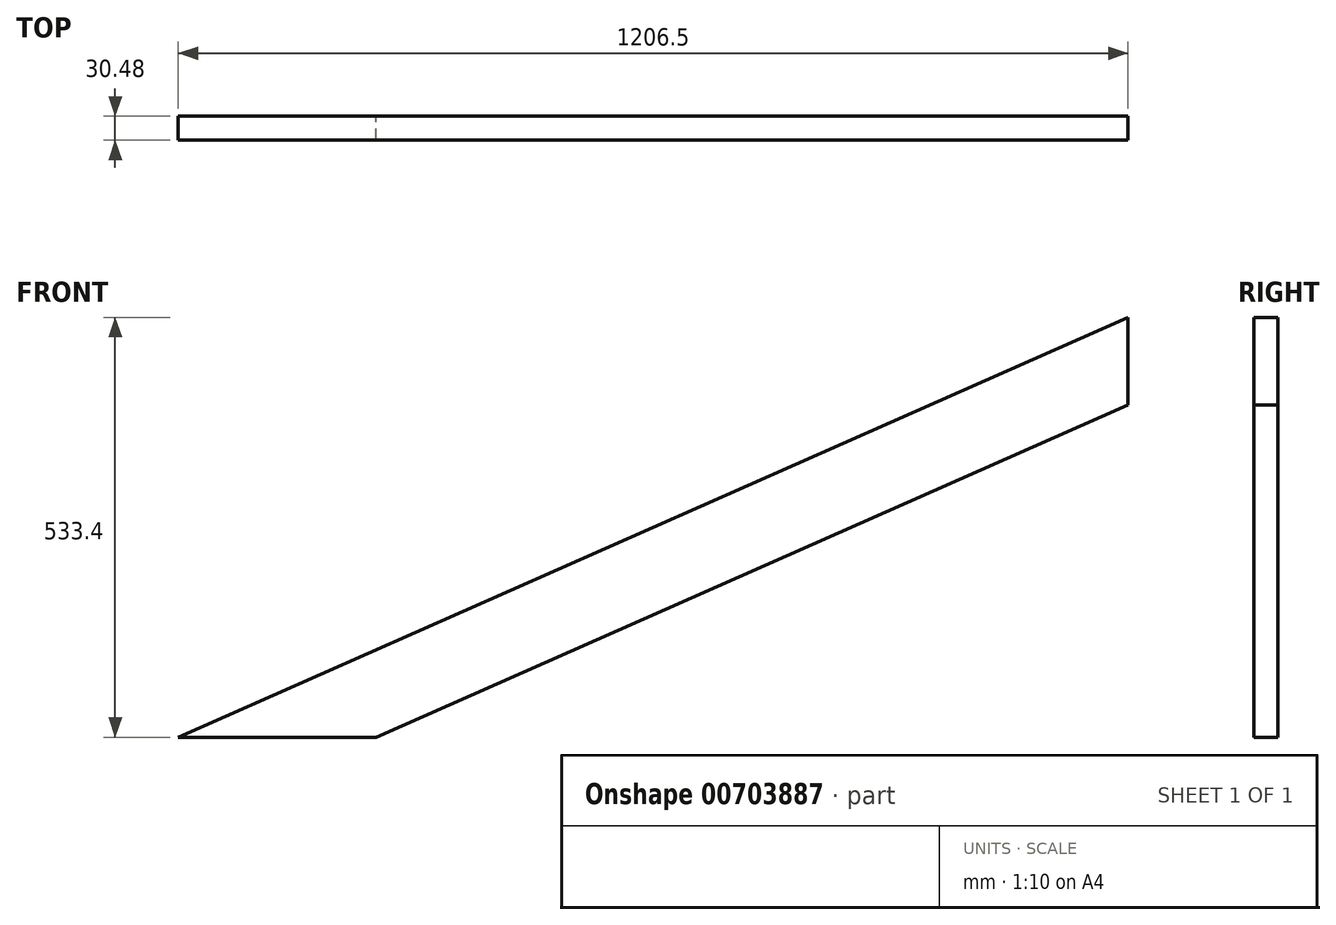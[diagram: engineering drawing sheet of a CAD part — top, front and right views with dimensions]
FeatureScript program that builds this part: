
annotation { "Feature Type Name" : "Feature", "Feature Type Description" : "" }
export const myFeature = defineFeature(function(context is Context, id is Id, definition is map)
    precondition{}
    {
        {
            var Q0;
            Q0=qCreatedBy(makeId("Front.planeOp"),FACE);
            var sketch = newSketch(context, id + "F0", { "sketchPlane" : qUnion([Q0])});
            skLineSegment(sketch, "E0", {"start": v(0, 0) * mm, "end": v(1206.5, 533.4) * mm});
            skLineSegment(sketch, "E1", {"start": v(1206.5, 422.31) * mm, "end": v(251.27, 0) * mm});
            skLineSegment(sketch, "E2", {"start": v(251.27, 0) * mm, "end": v(0, 0) * mm});
            skLineSegment(sketch, "E3", {"start": v(1206.5, 533.4) * mm, "end": v(1206.5, 422.31) * mm});
            skLineSegment(sketch, "E4", {"start": v(1206.5, 422.31) * mm, "end": v(1206.5, -331.81) * mm});
            skSolve(sketch);
        }
        {
            var Q0;
            Q0=qSketchRegion(id+"F0",true);
            extrude(context, id + "F1", {"entities" : qUnion([Q0]), "depth" : 30.48 * mm, "offsetDistance" : 30.48 * mm});
        }
    });
